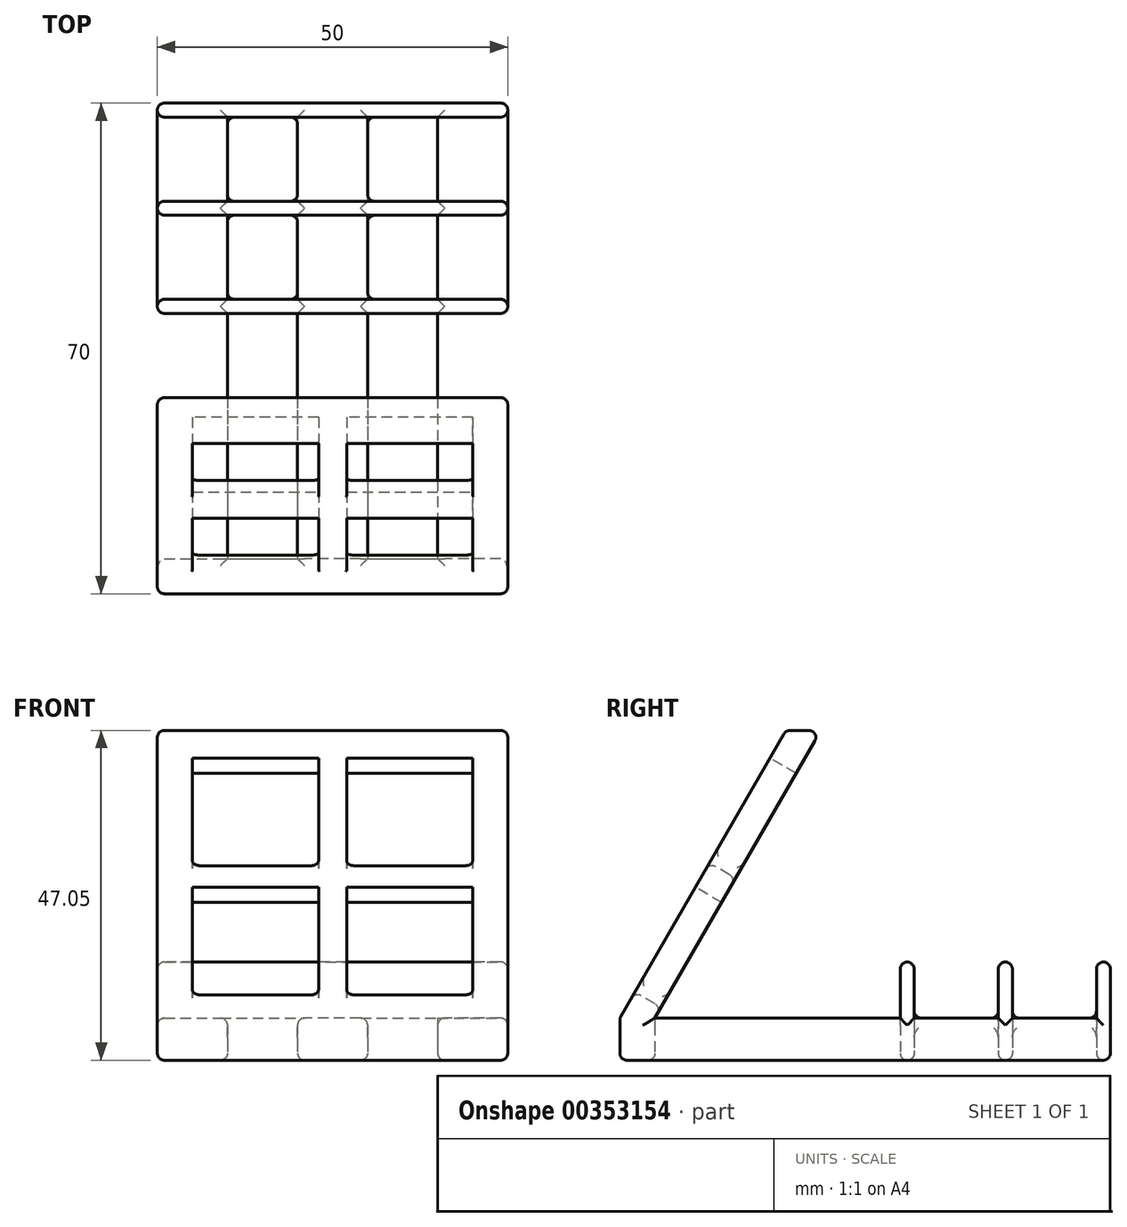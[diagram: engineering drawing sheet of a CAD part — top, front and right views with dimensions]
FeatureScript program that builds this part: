
annotation { "Feature Type Name" : "Feature", "Feature Type Description" : "" }
export const myFeature = defineFeature(function(context is Context, id is Id, definition is map)
    precondition{}
    {
        {
            var Q0;
            Q0=qCreatedBy(makeId("Top.planeOp"),FACE);
            var sketch = newSketch(context, id + "F0", { "sketchPlane" : qUnion([Q0])});
            skLineSegment(sketch, "E0.bottom", {"start": v(-23.48, 33.9) * mm, "end": v(26.52, 33.9) * mm});
            skLineSegment(sketch, "E0.top", {"start": v(-23.48, -36.1) * mm, "end": v(26.52, -36.1) * mm});
            skLineSegment(sketch, "E0.left", {"start": v(-23.48, 33.9) * mm, "end": v(-23.48, -36.1) * mm});
            skLineSegment(sketch, "E0.right", {"start": v(26.52, 33.9) * mm, "end": v(26.52, -36.1) * mm});
            skLineSegment(sketch, "E1", {"start": v(-23.48, 31.9) * mm, "end": v(26.52, 31.9) * mm});
            skLineSegment(sketch, "E2", {"start": v(-23.48, 19.9) * mm, "end": v(26.52, 19.9) * mm});
            skLineSegment(sketch, "E3", {"start": v(-23.48, 17.9) * mm, "end": v(26.52, 17.9) * mm});
            skLineSegment(sketch, "E4", {"start": v(-23.48, 5.9) * mm, "end": v(26.52, 5.9) * mm});
            skLineSegment(sketch, "E5", {"start": v(-23.48, -31.1) * mm, "end": v(26.52, -31.1) * mm});
            skLineSegment(sketch, "E6", {"start": v(-23.48, 3.9) * mm, "end": v(26.52, 3.9) * mm});
            skLineSegment(sketch, "E7", {"start": v(16.52, 33.9) * mm, "end": v(16.52, -36.1) * mm});
            skLineSegment(sketch, "E8", {"start": v(-13.48, 33.9) * mm, "end": v(-13.48, -36.1) * mm});
            skLineSegment(sketch, "E9.0", {"start": v(-3.48, 33.9) * mm, "end": v(-3.48, -36.1) * mm});
            skLineSegment(sketch, "E10.0", {"start": v(6.52, 33.9) * mm, "end": v(6.52, -36.1) * mm});
            skSolve(sketch);
        }
        {
            var Q0;
            {var subQ0=sQuery(id+"F0.wireOp",EDGE,"E9.0");var subQ1=sQuery(id+"F0.wireOp",EDGE,"E0.bottom");var subQ2=makeQuery(id+"F0.imprint","INTERSECT",VERTEX,{"derivedFrom":[subQ1,subQ0]});Q0=makeQuery(id+"F0.imprint","IMPRINT",FACE,{"disambiguationData":[TD([[makeQuery(id+"F0.imprint","IMPRINT",EDGE,{"disambiguationData":[TD([[subQ2,-1.0]])],"derivedFrom":subQ1}),-1.0]])]});}
            var Q1;
            {var subQ0=sQuery(id+"F0.wireOp",EDGE,"E9.0");var subQ1=sQuery(id+"F0.wireOp",EDGE,"E3");var subQ2=makeQuery(id+"F0.imprint","INTERSECT",VERTEX,{"derivedFrom":[subQ1,subQ0]});Q1=makeQuery(id+"F0.imprint","IMPRINT",FACE,{"disambiguationData":[TD([[makeQuery(id+"F0.imprint","IMPRINT",EDGE,{"disambiguationData":[TD([[subQ2,-1.0]])],"derivedFrom":subQ1}),-1.0]])]});}
            var Q2;
            {var subQ0=sQuery(id+"F0.wireOp",EDGE,"E10.0");var subQ1=sQuery(id+"F0.wireOp",EDGE,"E2");var subQ2=makeQuery(id+"F0.imprint","INTERSECT",VERTEX,{"derivedFrom":[subQ1,subQ0]});Q2=makeQuery(id+"F0.imprint","IMPRINT",FACE,{"disambiguationData":[TD([[makeQuery(id+"F0.imprint","IMPRINT",EDGE,{"disambiguationData":[TD([[subQ2,-1.0]])],"derivedFrom":subQ1}),-1.0]])]});}
            var Q3;
            {var subQ0=sQuery(id+"F0.wireOp",EDGE,"E5");var subQ1=sQuery(id+"F0.wireOp",EDGE,"E0.left");var subQ2=makeQuery(id+"F0.imprint","INTERSECT",VERTEX,{"derivedFrom":[subQ1,subQ0]});Q3=makeQuery(id+"F0.imprint","IMPRINT",FACE,{"disambiguationData":[TD([[makeQuery(id+"F0.imprint","IMPRINT",EDGE,{"disambiguationData":[TD([[subQ2,1.0]])],"derivedFrom":subQ1}),1.0]])]});}
            var Q4;
            {var subQ0=sQuery(id+"F0.wireOp",EDGE,"E0.left");var subQ1=sQuery(id+"F0.wireOp",EDGE,"E0.top");var subQ2=makeQuery(id+"F0.imprint","INTERSECT",VERTEX,{"derivedFrom":[subQ1,subQ0]});Q4=makeQuery(id+"F0.imprint","IMPRINT",FACE,{"disambiguationData":[TD([[makeQuery(id+"F0.imprint","IMPRINT",EDGE,{"disambiguationData":[TD([[subQ2,-1.0]])],"derivedFrom":subQ1}),1.0]])]});}
            var Q5;
            {var subQ0=sQuery(id+"F0.wireOp",EDGE,"E3");var subQ1=sQuery(id+"F0.wireOp",EDGE,"E0.left");var subQ2=makeQuery(id+"F0.imprint","INTERSECT",VERTEX,{"derivedFrom":[subQ1,subQ0]});Q5=makeQuery(id+"F0.imprint","IMPRINT",FACE,{"disambiguationData":[TD([[makeQuery(id+"F0.imprint","IMPRINT",EDGE,{"disambiguationData":[TD([[subQ2,-1.0]])],"derivedFrom":subQ1}),1.0]])]});}
            var Q6;
            {var subQ0=sQuery(id+"F0.wireOp",EDGE,"E8");var subQ1=sQuery(id+"F0.wireOp",EDGE,"E0.bottom");var subQ2=makeQuery(id+"F0.imprint","INTERSECT",VERTEX,{"derivedFrom":[subQ1,subQ0]});Q6=makeQuery(id+"F0.imprint","IMPRINT",FACE,{"disambiguationData":[TD([[makeQuery(id+"F0.imprint","IMPRINT",EDGE,{"disambiguationData":[TD([[subQ2,-1.0]])],"derivedFrom":subQ1}),-1.0]])]});}
            var Q7;
            {var subQ0=sQuery(id+"F0.wireOp",EDGE,"E2");var subQ1=sQuery(id+"F0.wireOp",EDGE,"E0.right");var subQ2=makeQuery(id+"F0.imprint","INTERSECT",VERTEX,{"derivedFrom":[subQ1,subQ0]});Q7=makeQuery(id+"F0.imprint","IMPRINT",FACE,{"disambiguationData":[TD([[makeQuery(id+"F0.imprint","IMPRINT",EDGE,{"disambiguationData":[TD([[subQ2,-1.0]])],"derivedFrom":subQ1}),-1.0]])]});}
            var Q8;
            {var subQ0=sQuery(id+"F0.wireOp",EDGE,"E4");var subQ1=sQuery(id+"F0.wireOp",EDGE,"E0.right");var subQ2=makeQuery(id+"F0.imprint","INTERSECT",VERTEX,{"derivedFrom":[subQ1,subQ0]});Q8=makeQuery(id+"F0.imprint","IMPRINT",FACE,{"disambiguationData":[TD([[makeQuery(id+"F0.imprint","IMPRINT",EDGE,{"disambiguationData":[TD([[subQ2,-1.0]])],"derivedFrom":subQ1}),-1.0]])]});}
            var Q9;
            {var subQ0=sQuery(id+"F0.wireOp",EDGE,"E3");var subQ1=sQuery(id+"F0.wireOp",EDGE,"E0.right");var subQ2=makeQuery(id+"F0.imprint","INTERSECT",VERTEX,{"derivedFrom":[subQ1,subQ0]});Q9=makeQuery(id+"F0.imprint","IMPRINT",FACE,{"disambiguationData":[TD([[makeQuery(id+"F0.imprint","IMPRINT",EDGE,{"disambiguationData":[TD([[subQ2,-1.0]])],"derivedFrom":subQ1}),-1.0]])]});}
            var Q10;
            {var subQ0=sQuery(id+"F0.wireOp",EDGE,"E2");var subQ1=sQuery(id+"F0.wireOp",EDGE,"E0.left");var subQ2=makeQuery(id+"F0.imprint","INTERSECT",VERTEX,{"derivedFrom":[subQ1,subQ0]});Q10=makeQuery(id+"F0.imprint","IMPRINT",FACE,{"disambiguationData":[TD([[makeQuery(id+"F0.imprint","IMPRINT",EDGE,{"disambiguationData":[TD([[subQ2,-1.0]])],"derivedFrom":subQ1}),1.0]])]});}
            var Q11;
            {var subQ0=sQuery(id+"F0.wireOp",EDGE,"E7");var subQ1=sQuery(id+"F0.wireOp",EDGE,"E0.top");var subQ2=makeQuery(id+"F0.imprint","INTERSECT",VERTEX,{"derivedFrom":[subQ1,subQ0]});Q11=makeQuery(id+"F0.imprint","IMPRINT",FACE,{"disambiguationData":[TD([[makeQuery(id+"F0.imprint","IMPRINT",EDGE,{"disambiguationData":[TD([[subQ2,1.0]])],"derivedFrom":subQ1}),1.0]])]});}
            var Q12;
            {var subQ0=sQuery(id+"F0.wireOp",EDGE,"E9.0");var subQ1=sQuery(id+"F0.wireOp",EDGE,"E0.top");var subQ2=makeQuery(id+"F0.imprint","INTERSECT",VERTEX,{"derivedFrom":[subQ1,subQ0]});Q12=makeQuery(id+"F0.imprint","IMPRINT",FACE,{"disambiguationData":[TD([[makeQuery(id+"F0.imprint","IMPRINT",EDGE,{"disambiguationData":[TD([[subQ2,-1.0]])],"derivedFrom":subQ1}),1.0]])]});}
            var Q13;
            {var subQ0=sQuery(id+"F0.wireOp",EDGE,"E10.0");var subQ1=sQuery(id+"F0.wireOp",EDGE,"E4");var subQ2=makeQuery(id+"F0.imprint","INTERSECT",VERTEX,{"derivedFrom":[subQ1,subQ0]});Q13=makeQuery(id+"F0.imprint","IMPRINT",FACE,{"disambiguationData":[TD([[makeQuery(id+"F0.imprint","IMPRINT",EDGE,{"disambiguationData":[TD([[subQ2,-1.0]])],"derivedFrom":subQ1}),-1.0]])]});}
            var Q14;
            {var subQ0=sQuery(id+"F0.wireOp",EDGE,"E0.right");var subQ1=sQuery(id+"F0.wireOp",EDGE,"E0.top");var subQ2=makeQuery(id+"F0.imprint","INTERSECT",VERTEX,{"derivedFrom":[subQ1,subQ0]});Q14=makeQuery(id+"F0.imprint","IMPRINT",FACE,{"disambiguationData":[TD([[makeQuery(id+"F0.imprint","IMPRINT",EDGE,{"disambiguationData":[TD([[subQ2,1.0]])],"derivedFrom":subQ1}),1.0]])]});}
            var Q15;
            {var subQ0=sQuery(id+"F0.wireOp",EDGE,"E1");var subQ1=sQuery(id+"F0.wireOp",EDGE,"E0.left");var subQ2=makeQuery(id+"F0.imprint","INTERSECT",VERTEX,{"derivedFrom":[subQ1,subQ0]});Q15=makeQuery(id+"F0.imprint","IMPRINT",FACE,{"disambiguationData":[TD([[makeQuery(id+"F0.imprint","IMPRINT",EDGE,{"disambiguationData":[TD([[subQ2,-1.0]])],"derivedFrom":subQ1}),1.0]])]});}
            var Q16;
            {var subQ0=sQuery(id+"F0.wireOp",EDGE,"E9.0");var subQ1=sQuery(id+"F0.wireOp",EDGE,"E5");var subQ2=makeQuery(id+"F0.imprint","INTERSECT",VERTEX,{"derivedFrom":[subQ1,subQ0]});Q16=makeQuery(id+"F0.imprint","IMPRINT",FACE,{"disambiguationData":[TD([[makeQuery(id+"F0.imprint","IMPRINT",EDGE,{"disambiguationData":[TD([[subQ2,-1.0]])],"derivedFrom":subQ1}),1.0]])]});}
            var Q17;
            {var subQ0=sQuery(id+"F0.wireOp",EDGE,"E8");var subQ1=sQuery(id+"F0.wireOp",EDGE,"E2");var subQ2=makeQuery(id+"F0.imprint","INTERSECT",VERTEX,{"derivedFrom":[subQ1,subQ0]});Q17=makeQuery(id+"F0.imprint","IMPRINT",FACE,{"disambiguationData":[TD([[makeQuery(id+"F0.imprint","IMPRINT",EDGE,{"disambiguationData":[TD([[subQ2,-1.0]])],"derivedFrom":subQ1}),-1.0]])]});}
            var Q18;
            {var subQ0=sQuery(id+"F0.wireOp",EDGE,"E8");var subQ1=sQuery(id+"F0.wireOp",EDGE,"E0.top");var subQ2=makeQuery(id+"F0.imprint","INTERSECT",VERTEX,{"derivedFrom":[subQ1,subQ0]});Q18=makeQuery(id+"F0.imprint","IMPRINT",FACE,{"disambiguationData":[TD([[makeQuery(id+"F0.imprint","IMPRINT",EDGE,{"disambiguationData":[TD([[subQ2,-1.0]])],"derivedFrom":subQ1}),1.0]])]});}
            var Q19;
            {var subQ0=sQuery(id+"F0.wireOp",EDGE,"E9.0");var subQ1=sQuery(id+"F0.wireOp",EDGE,"E4");var subQ2=makeQuery(id+"F0.imprint","INTERSECT",VERTEX,{"derivedFrom":[subQ1,subQ0]});Q19=makeQuery(id+"F0.imprint","IMPRINT",FACE,{"disambiguationData":[TD([[makeQuery(id+"F0.imprint","IMPRINT",EDGE,{"disambiguationData":[TD([[subQ2,-1.0]])],"derivedFrom":subQ1}),-1.0]])]});}
            var Q20;
            {var subQ0=sQuery(id+"F0.wireOp",EDGE,"E9.0");var subQ1=sQuery(id+"F0.wireOp",EDGE,"E1");var subQ2=makeQuery(id+"F0.imprint","INTERSECT",VERTEX,{"derivedFrom":[subQ1,subQ0]});Q20=makeQuery(id+"F0.imprint","IMPRINT",FACE,{"disambiguationData":[TD([[makeQuery(id+"F0.imprint","IMPRINT",EDGE,{"disambiguationData":[TD([[subQ2,-1.0]])],"derivedFrom":subQ1}),-1.0]])]});}
            var Q21;
            {var subQ0=sQuery(id+"F0.wireOp",EDGE,"E5");var subQ1=sQuery(id+"F0.wireOp",EDGE,"E0.right");var subQ2=makeQuery(id+"F0.imprint","INTERSECT",VERTEX,{"derivedFrom":[subQ1,subQ0]});Q21=makeQuery(id+"F0.imprint","IMPRINT",FACE,{"disambiguationData":[TD([[makeQuery(id+"F0.imprint","IMPRINT",EDGE,{"disambiguationData":[TD([[subQ2,1.0]])],"derivedFrom":subQ1}),-1.0]])]});}
            var Q22;
            {var subQ0=sQuery(id+"F0.wireOp",EDGE,"E4");var subQ1=sQuery(id+"F0.wireOp",EDGE,"E0.left");var subQ2=makeQuery(id+"F0.imprint","INTERSECT",VERTEX,{"derivedFrom":[subQ1,subQ0]});Q22=makeQuery(id+"F0.imprint","IMPRINT",FACE,{"disambiguationData":[TD([[makeQuery(id+"F0.imprint","IMPRINT",EDGE,{"disambiguationData":[TD([[subQ2,-1.0]])],"derivedFrom":subQ1}),1.0]])]});}
            var Q23;
            {var subQ0=sQuery(id+"F0.wireOp",EDGE,"E8");var subQ1=sQuery(id+"F0.wireOp",EDGE,"E4");var subQ2=makeQuery(id+"F0.imprint","INTERSECT",VERTEX,{"derivedFrom":[subQ1,subQ0]});Q23=makeQuery(id+"F0.imprint","IMPRINT",FACE,{"disambiguationData":[TD([[makeQuery(id+"F0.imprint","IMPRINT",EDGE,{"disambiguationData":[TD([[subQ2,-1.0]])],"derivedFrom":subQ1}),-1.0]])]});}
            var Q24;
            {var subQ0=sQuery(id+"F0.wireOp",EDGE,"E9.0");var subQ1=sQuery(id+"F0.wireOp",EDGE,"E2");var subQ2=makeQuery(id+"F0.imprint","INTERSECT",VERTEX,{"derivedFrom":[subQ1,subQ0]});Q24=makeQuery(id+"F0.imprint","IMPRINT",FACE,{"disambiguationData":[TD([[makeQuery(id+"F0.imprint","IMPRINT",EDGE,{"disambiguationData":[TD([[subQ2,-1.0]])],"derivedFrom":subQ1}),-1.0]])]});}
            var Q25;
            {var subQ0=sQuery(id+"F0.wireOp",EDGE,"E1");var subQ1=sQuery(id+"F0.wireOp",EDGE,"E0.right");var subQ2=makeQuery(id+"F0.imprint","INTERSECT",VERTEX,{"derivedFrom":[subQ1,subQ0]});Q25=makeQuery(id+"F0.imprint","IMPRINT",FACE,{"disambiguationData":[TD([[makeQuery(id+"F0.imprint","IMPRINT",EDGE,{"disambiguationData":[TD([[subQ2,-1.0]])],"derivedFrom":subQ1}),-1.0]])]});}
            var Q26;
            {var subQ0=sQuery(id+"F0.wireOp",EDGE,"E0.left");var subQ1=sQuery(id+"F0.wireOp",EDGE,"E0.bottom");var subQ2=makeQuery(id+"F0.imprint","INTERSECT",VERTEX,{"derivedFrom":[subQ1,subQ0]});Q26=makeQuery(id+"F0.imprint","IMPRINT",FACE,{"disambiguationData":[TD([[makeQuery(id+"F0.imprint","IMPRINT",EDGE,{"disambiguationData":[TD([[subQ2,-1.0]])],"derivedFrom":subQ1}),-1.0]])]});}
            var Q27;
            {var subQ0=sQuery(id+"F0.wireOp",EDGE,"E0.right");var subQ1=sQuery(id+"F0.wireOp",EDGE,"E0.bottom");var subQ2=makeQuery(id+"F0.imprint","INTERSECT",VERTEX,{"derivedFrom":[subQ1,subQ0]});Q27=makeQuery(id+"F0.imprint","IMPRINT",FACE,{"disambiguationData":[TD([[makeQuery(id+"F0.imprint","IMPRINT",EDGE,{"disambiguationData":[TD([[subQ2,1.0]])],"derivedFrom":subQ1}),-1.0]])]});}
            var Q28;
            {var subQ0=sQuery(id+"F0.wireOp",EDGE,"E7");var subQ1=sQuery(id+"F0.wireOp",EDGE,"E0.bottom");var subQ2=makeQuery(id+"F0.imprint","INTERSECT",VERTEX,{"derivedFrom":[subQ1,subQ0]});Q28=makeQuery(id+"F0.imprint","IMPRINT",FACE,{"disambiguationData":[TD([[makeQuery(id+"F0.imprint","IMPRINT",EDGE,{"disambiguationData":[TD([[subQ2,1.0]])],"derivedFrom":subQ1}),-1.0]])]});}
            extrude(context, id + "F1", {"entities" : qUnion([Q0, Q1, Q2, Q3, Q4, Q5, Q6, Q7, Q8, Q9, Q10, Q11, Q12, Q13, Q14, Q15, Q16, Q17, Q18, Q19, Q20, Q21, Q22, Q23, Q24, Q25, Q26, Q27, Q28]), "depth" : 6 * mm});
        }
        {
            var Q0;
            {var subQ0=sQuery(id+"F0.wireOp",EDGE,"E8");var subQ1=sQuery(id+"F0.wireOp",EDGE,"E0.bottom");var subQ2=makeQuery(id+"F0.imprint","INTERSECT",VERTEX,{"derivedFrom":[subQ1,subQ0]});Q0=makeQuery(id+"F0.imprint","IMPRINT",FACE,{"disambiguationData":[TD([[makeQuery(id+"F0.imprint","IMPRINT",EDGE,{"disambiguationData":[TD([[subQ2,-1.0]])],"derivedFrom":subQ1}),-1.0]])]});}
            var Q1;
            {var subQ0=sQuery(id+"F0.wireOp",EDGE,"E0.left");var subQ1=sQuery(id+"F0.wireOp",EDGE,"E0.bottom");var subQ2=makeQuery(id+"F0.imprint","INTERSECT",VERTEX,{"derivedFrom":[subQ1,subQ0]});Q1=makeQuery(id+"F0.imprint","IMPRINT",FACE,{"disambiguationData":[TD([[makeQuery(id+"F0.imprint","IMPRINT",EDGE,{"disambiguationData":[TD([[subQ2,-1.0]])],"derivedFrom":subQ1}),-1.0]])]});}
            var Q2;
            {var subQ0=sQuery(id+"F0.wireOp",EDGE,"E7");var subQ1=sQuery(id+"F0.wireOp",EDGE,"E0.bottom");var subQ2=makeQuery(id+"F0.imprint","INTERSECT",VERTEX,{"derivedFrom":[subQ1,subQ0]});Q2=makeQuery(id+"F0.imprint","IMPRINT",FACE,{"disambiguationData":[TD([[makeQuery(id+"F0.imprint","IMPRINT",EDGE,{"disambiguationData":[TD([[subQ2,1.0]])],"derivedFrom":subQ1}),-1.0]])]});}
            var Q3;
            {var subQ0=sQuery(id+"F0.wireOp",EDGE,"E9.0");var subQ1=sQuery(id+"F0.wireOp",EDGE,"E0.bottom");var subQ2=makeQuery(id+"F0.imprint","INTERSECT",VERTEX,{"derivedFrom":[subQ1,subQ0]});Q3=makeQuery(id+"F0.imprint","IMPRINT",FACE,{"disambiguationData":[TD([[makeQuery(id+"F0.imprint","IMPRINT",EDGE,{"disambiguationData":[TD([[subQ2,-1.0]])],"derivedFrom":subQ1}),-1.0]])]});}
            var Q4;
            {var subQ0=sQuery(id+"F0.wireOp",EDGE,"E0.right");var subQ1=sQuery(id+"F0.wireOp",EDGE,"E0.bottom");var subQ2=makeQuery(id+"F0.imprint","INTERSECT",VERTEX,{"derivedFrom":[subQ1,subQ0]});Q4=makeQuery(id+"F0.imprint","IMPRINT",FACE,{"disambiguationData":[TD([[makeQuery(id+"F0.imprint","IMPRINT",EDGE,{"disambiguationData":[TD([[subQ2,1.0]])],"derivedFrom":subQ1}),-1.0]])]});}
            var Q5;
            {var subQ0=sQuery(id+"F0.wireOp",EDGE,"E9.0");var subQ1=sQuery(id+"F0.wireOp",EDGE,"E2");var subQ2=makeQuery(id+"F0.imprint","INTERSECT",VERTEX,{"derivedFrom":[subQ1,subQ0]});Q5=makeQuery(id+"F0.imprint","IMPRINT",FACE,{"disambiguationData":[TD([[makeQuery(id+"F0.imprint","IMPRINT",EDGE,{"disambiguationData":[TD([[subQ2,-1.0]])],"derivedFrom":subQ1}),-1.0]])]});}
            var Q6;
            {var subQ0=sQuery(id+"F0.wireOp",EDGE,"E10.0");var subQ1=sQuery(id+"F0.wireOp",EDGE,"E2");var subQ2=makeQuery(id+"F0.imprint","INTERSECT",VERTEX,{"derivedFrom":[subQ1,subQ0]});Q6=makeQuery(id+"F0.imprint","IMPRINT",FACE,{"disambiguationData":[TD([[makeQuery(id+"F0.imprint","IMPRINT",EDGE,{"disambiguationData":[TD([[subQ2,-1.0]])],"derivedFrom":subQ1}),-1.0]])]});}
            var Q7;
            {var subQ0=sQuery(id+"F0.wireOp",EDGE,"E2");var subQ1=sQuery(id+"F0.wireOp",EDGE,"E0.right");var subQ2=makeQuery(id+"F0.imprint","INTERSECT",VERTEX,{"derivedFrom":[subQ1,subQ0]});Q7=makeQuery(id+"F0.imprint","IMPRINT",FACE,{"disambiguationData":[TD([[makeQuery(id+"F0.imprint","IMPRINT",EDGE,{"disambiguationData":[TD([[subQ2,-1.0]])],"derivedFrom":subQ1}),-1.0]])]});}
            var Q8;
            {var subQ0=sQuery(id+"F0.wireOp",EDGE,"E8");var subQ1=sQuery(id+"F0.wireOp",EDGE,"E2");var subQ2=makeQuery(id+"F0.imprint","INTERSECT",VERTEX,{"derivedFrom":[subQ1,subQ0]});Q8=makeQuery(id+"F0.imprint","IMPRINT",FACE,{"disambiguationData":[TD([[makeQuery(id+"F0.imprint","IMPRINT",EDGE,{"disambiguationData":[TD([[subQ2,-1.0]])],"derivedFrom":subQ1}),-1.0]])]});}
            var Q9;
            {var subQ0=sQuery(id+"F0.wireOp",EDGE,"E2");var subQ1=sQuery(id+"F0.wireOp",EDGE,"E0.left");var subQ2=makeQuery(id+"F0.imprint","INTERSECT",VERTEX,{"derivedFrom":[subQ1,subQ0]});Q9=makeQuery(id+"F0.imprint","IMPRINT",FACE,{"disambiguationData":[TD([[makeQuery(id+"F0.imprint","IMPRINT",EDGE,{"disambiguationData":[TD([[subQ2,-1.0]])],"derivedFrom":subQ1}),1.0]])]});}
            var Q10;
            {var subQ0=sQuery(id+"F0.wireOp",EDGE,"E4");var subQ1=sQuery(id+"F0.wireOp",EDGE,"E0.left");var subQ2=makeQuery(id+"F0.imprint","INTERSECT",VERTEX,{"derivedFrom":[subQ1,subQ0]});Q10=makeQuery(id+"F0.imprint","IMPRINT",FACE,{"disambiguationData":[TD([[makeQuery(id+"F0.imprint","IMPRINT",EDGE,{"disambiguationData":[TD([[subQ2,-1.0]])],"derivedFrom":subQ1}),1.0]])]});}
            var Q11;
            {var subQ0=sQuery(id+"F0.wireOp",EDGE,"E8");var subQ1=sQuery(id+"F0.wireOp",EDGE,"E4");var subQ2=makeQuery(id+"F0.imprint","INTERSECT",VERTEX,{"derivedFrom":[subQ1,subQ0]});Q11=makeQuery(id+"F0.imprint","IMPRINT",FACE,{"disambiguationData":[TD([[makeQuery(id+"F0.imprint","IMPRINT",EDGE,{"disambiguationData":[TD([[subQ2,-1.0]])],"derivedFrom":subQ1}),-1.0]])]});}
            var Q12;
            {var subQ0=sQuery(id+"F0.wireOp",EDGE,"E9.0");var subQ1=sQuery(id+"F0.wireOp",EDGE,"E4");var subQ2=makeQuery(id+"F0.imprint","INTERSECT",VERTEX,{"derivedFrom":[subQ1,subQ0]});Q12=makeQuery(id+"F0.imprint","IMPRINT",FACE,{"disambiguationData":[TD([[makeQuery(id+"F0.imprint","IMPRINT",EDGE,{"disambiguationData":[TD([[subQ2,-1.0]])],"derivedFrom":subQ1}),-1.0]])]});}
            var Q13;
            {var subQ0=sQuery(id+"F0.wireOp",EDGE,"E10.0");var subQ1=sQuery(id+"F0.wireOp",EDGE,"E4");var subQ2=makeQuery(id+"F0.imprint","INTERSECT",VERTEX,{"derivedFrom":[subQ1,subQ0]});Q13=makeQuery(id+"F0.imprint","IMPRINT",FACE,{"disambiguationData":[TD([[makeQuery(id+"F0.imprint","IMPRINT",EDGE,{"disambiguationData":[TD([[subQ2,-1.0]])],"derivedFrom":subQ1}),-1.0]])]});}
            var Q14;
            {var subQ0=sQuery(id+"F0.wireOp",EDGE,"E4");var subQ1=sQuery(id+"F0.wireOp",EDGE,"E0.right");var subQ2=makeQuery(id+"F0.imprint","INTERSECT",VERTEX,{"derivedFrom":[subQ1,subQ0]});Q14=makeQuery(id+"F0.imprint","IMPRINT",FACE,{"disambiguationData":[TD([[makeQuery(id+"F0.imprint","IMPRINT",EDGE,{"disambiguationData":[TD([[subQ2,-1.0]])],"derivedFrom":subQ1}),-1.0]])]});}
            extrude(context, id + "F2", {"entities" : qUnion([Q0, Q1, Q2, Q3, Q4, Q5, Q6, Q7, Q8, Q9, Q10, Q11, Q12, Q13, Q14]), "depth" : 14 * mm});
        }
        {
            var Q0;
            Q0=makeQuery(id+"F1.opExtrude","SWEPT_FACE",FACE,{"disambiguationData":[OSD([sQuery(id+"F0.wireOp",EDGE,"E0.left")])]});
            var sketch = newSketch(context, id + "F3", { "sketchPlane" : qUnion([Q0])});
            skLineSegment(sketch, "E11", {"start": v(36.1, 6) * mm, "end": v(12.4, 47.05) * mm});
            skSolve(sketch);
        }
        {
            var Q0;
            Q0=qCreatedBy(makeId("Top.planeOp"),FACE);
            var Q1;
            Q1=sQuery(id+"F3.wireOp",VERTEX,"E11.end");
            cPlane(context, id + "F4", {"entities" : qUnion([Q0, Q1]), "cplaneType" : CPlaneType.PLANE_POINT, "offset" : 25 * mm, "width" : 150 * mm, "height" : 150 * mm});
        }
        {
            var Q0;
            Q0=qCreatedBy(id+"F4.planeOp",FACE);
            var sketch = newSketch(context, id + "F5", { "sketchPlane" : qUnion([Q0])});
            skLineSegment(sketch, "E12.0", {"start": v(-23.48, -7.4) * mm, "end": v(-23.48, -12.4) * mm});
            skLineSegment(sketch, "E12.1", {"start": v(26.52, -7.4) * mm, "end": v(26.52, -12.4) * mm});
            skLineSegment(sketch, "E13", {"start": v(-23.48, -12.4) * mm, "end": v(26.52, -12.4) * mm});
            skLineSegment(sketch, "E14", {"start": v(26.52, -7.4) * mm, "end": v(-23.48, -7.4) * mm});
            skPoint(sketch, "E15.orphan", {"position": v(-23.48, 33.9) * mm});
            skPoint(sketch, "E16.orphan", {"position": v(-23.48, -36.1) * mm});
            skPoint(sketch, "E17.orphan", {"position": v(26.52, -36.1) * mm});
            skPoint(sketch, "E18.orphan", {"position": v(26.52, 33.9) * mm});
            skSolve(sketch);
        }
        {
            var Q0;
            Q0=makeQuery(id+"F1.opExtrude","CAP_FACE",FACE,{"disambiguationData":[OSD([sQuery(id+"F0.wireOp",EDGE,"E0.bottom"),sQuery(id+"F0.wireOp",EDGE,"E0.top"),sQuery(id+"F0.wireOp",EDGE,"E0.left"),sQuery(id+"F0.wireOp",EDGE,"E0.right"),sQuery(id+"F0.wireOp",EDGE,"E1"),sQuery(id+"F0.wireOp",EDGE,"E2"),sQuery(id+"F0.wireOp",EDGE,"E3"),sQuery(id+"F0.wireOp",EDGE,"E4"),sQuery(id+"F0.wireOp",EDGE,"E5"),sQuery(id+"F0.wireOp",EDGE,"E6"),sQuery(id+"F0.wireOp",EDGE,"E7"),sQuery(id+"F0.wireOp",EDGE,"E8"),sQuery(id+"F0.wireOp",EDGE,"E9.0"),sQuery(id+"F0.wireOp",EDGE,"E10.0")])],"isStart":false});
            var sketch = newSketch(context, id + "F6", { "sketchPlane" : qUnion([Q0])});
            skLineSegment(sketch, "E19.0", {"start": v(-23.48, -31.1) * mm, "end": v(26.52, -31.1) * mm});
            skLineSegment(sketch, "E19.1", {"start": v(-23.48, -36.1) * mm, "end": v(26.52, -36.1) * mm});
            skLineSegment(sketch, "E19.2", {"start": v(-23.48, -31.1) * mm, "end": v(-23.48, -36.1) * mm});
            skLineSegment(sketch, "E19.3", {"start": v(26.52, -31.1) * mm, "end": v(26.52, -36.1) * mm});
            skPoint(sketch, "E20.orphan", {"position": v(-23.48, 33.9) * mm});
            skPoint(sketch, "E21.orphan", {"position": v(26.52, 33.9) * mm});
            skSolve(sketch);
        }
        {
            var Q0;
            Q0=makeQuery(id+"F5.imprint","IMPRINT",FACE,{"disambiguationData":[TD([[makeQuery(id+"F5.imprint","IMPRINT",EDGE,{"derivedFrom":sQuery(id+"F5.wireOp",EDGE,"E12.0")}),1.0]])]});
            var Q1;
            Q1=makeQuery(id+"F6.imprint","IMPRINT",FACE,{"disambiguationData":[TD([[makeQuery(id+"F6.imprint","IMPRINT",EDGE,{"derivedFrom":sQuery(id+"F6.wireOp",EDGE,"E19.1")}),1.0]])]});
            var Q2;
            Q2=sQuery(id+"F3.wireOp",EDGE,"E11");
            loft(context, id + "F7", {"sheetProfilesArray" : [{ "sheetProfileEntities" : qUnion([Q0]) }, { "sheetProfileEntities" : qUnion([Q1]) }], "guidesArray" : [{ "guideEntities" : qUnion([Q2]), "guideDerivativeType" : LoftGuideDerivativeType.DEFAULT, "guideDerivativeMagnitude" : 1 }]});
        }
        {
            var Q0;
            Q0=makeQuery(id+"F2.opExtrude","SWEPT_BODY",BODY,{"disambiguationData":[OSD([sQuery(id+"F0.wireOp",EDGE,"E0.left"),sQuery(id+"F0.wireOp",EDGE,"E0.right"),sQuery(id+"F0.wireOp",EDGE,"E4"),sQuery(id+"F0.wireOp",EDGE,"E6")])]});
            var Q1;
            Q1=makeQuery(id+"F2.opExtrude","SWEPT_BODY",BODY,{"disambiguationData":[OSD([sQuery(id+"F0.wireOp",EDGE,"E0.left"),sQuery(id+"F0.wireOp",EDGE,"E0.right"),sQuery(id+"F0.wireOp",EDGE,"E2"),sQuery(id+"F0.wireOp",EDGE,"E3")])]});
            var Q2;
            Q2=makeQuery(id+"F7.opLoft","SWEPT_BODY",BODY,{"disambiguationData":[OSD([makeQuery(id+"F5.imprint","IMPRINT",FACE,{"disambiguationData":[TD([[makeQuery(id+"F5.imprint","IMPRINT",EDGE,{"derivedFrom":sQuery(id+"F5.wireOp",EDGE,"E12.0")}),1.0]])]}),makeQuery(id+"F6.imprint","IMPRINT",FACE,{"disambiguationData":[TD([[makeQuery(id+"F6.imprint","IMPRINT",EDGE,{"derivedFrom":sQuery(id+"F6.wireOp",EDGE,"E19.1")}),1.0]])]})])]});
            var Q3;
            Q3=makeQuery(id+"F1.opExtrude","SWEPT_BODY",BODY,{"disambiguationData":[OSD([sQuery(id+"F0.wireOp",EDGE,"E0.bottom"),sQuery(id+"F0.wireOp",EDGE,"E0.top"),sQuery(id+"F0.wireOp",EDGE,"E0.left"),sQuery(id+"F0.wireOp",EDGE,"E0.right"),sQuery(id+"F0.wireOp",EDGE,"E1"),sQuery(id+"F0.wireOp",EDGE,"E2"),sQuery(id+"F0.wireOp",EDGE,"E3"),sQuery(id+"F0.wireOp",EDGE,"E4"),sQuery(id+"F0.wireOp",EDGE,"E5"),sQuery(id+"F0.wireOp",EDGE,"E6"),sQuery(id+"F0.wireOp",EDGE,"E7"),sQuery(id+"F0.wireOp",EDGE,"E8"),sQuery(id+"F0.wireOp",EDGE,"E9.0"),sQuery(id+"F0.wireOp",EDGE,"E10.0")])]});
            var Q4;
            Q4=makeQuery(id+"F2.opExtrude","SWEPT_BODY",BODY,{"disambiguationData":[OSD([sQuery(id+"F0.wireOp",EDGE,"E0.bottom"),sQuery(id+"F0.wireOp",EDGE,"E0.left"),sQuery(id+"F0.wireOp",EDGE,"E0.right"),sQuery(id+"F0.wireOp",EDGE,"E1")])]});
            booleanBodies(context, id + "F8", {"operationType" : BooleanOperationType.UNION, "tools" : qUnion([Q0, Q1, Q2, Q3, Q4])});
        }
        {
            var Q0;
            Q0=makeQuery(id+"F7.opLoft","CAP_FACE",FACE,{"disambiguationData":[OSD([makeQuery(id+"F5.imprint","IMPRINT",FACE,{"disambiguationData":[TD([[makeQuery(id+"F5.imprint","IMPRINT",EDGE,{"derivedFrom":sQuery(id+"F5.wireOp",EDGE,"E12.0")}),1.0]])]})])],"isStart":true});
            var Q1;
            Q1=makeQuery(id+"F2.opExtrude","CAP_FACE",FACE,{"disambiguationData":[OSD([sQuery(id+"F0.wireOp",EDGE,"E0.bottom"),sQuery(id+"F0.wireOp",EDGE,"E0.left"),sQuery(id+"F0.wireOp",EDGE,"E0.right"),sQuery(id+"F0.wireOp",EDGE,"E1")])],"isStart":false});
            var Q2;
            Q2=makeQuery(id+"F2.opExtrude","CAP_FACE",FACE,{"disambiguationData":[OSD([sQuery(id+"F0.wireOp",EDGE,"E0.left"),sQuery(id+"F0.wireOp",EDGE,"E0.right"),sQuery(id+"F0.wireOp",EDGE,"E4"),sQuery(id+"F0.wireOp",EDGE,"E6")])],"isStart":false});
            var Q3;
            Q3=makeQuery(id+"F7.opLoft","SWEPT_FACE",FACE,{"disambiguationData":[OSD([sQuery(id+"F5.wireOp",EDGE,"E12.0"),sQuery(id+"F5.wireOp",EDGE,"E12.1"),sQuery(id+"F5.wireOp",EDGE,"E13"),sQuery(id+"F6.wireOp",EDGE,"E19.1"),sQuery(id+"F6.wireOp",EDGE,"E19.2"),sQuery(id+"F6.wireOp",EDGE,"E19.3")])]});
            var Q4;
            {var subQ0=sQuery(id+"F0.wireOp",EDGE,"E0.right");Q4=makeQuery(id+"F8.opBoolean","MERGE",FACE,{"derivedFrom":[makeQuery(id+"F1.opExtrude","SWEPT_FACE",FACE,{"disambiguationData":[OSD([subQ0])]}),makeQuery(id+"F2.opExtrude","SWEPT_FACE",FACE,{"disambiguationData":[OSD([subQ0]),TDD([makeQuery(id+"F0.imprint","IMPRINT",EDGE,{"disambiguationData":[TD([[makeQuery(id+"F0.imprint","INTERSECT",VERTEX,{"derivedFrom":[sQuery(id+"F0.wireOp",EDGE,"E0.bottom"),subQ0]}),-1.0]])],"derivedFrom":subQ0})])]}),makeQuery(id+"F2.opExtrude","SWEPT_FACE",FACE,{"disambiguationData":[OSD([subQ0]),TDD([makeQuery(id+"F0.imprint","IMPRINT",EDGE,{"disambiguationData":[TD([[makeQuery(id+"F0.imprint","INTERSECT",VERTEX,{"derivedFrom":[subQ0,sQuery(id+"F0.wireOp",EDGE,"E2")]}),-1.0]])],"derivedFrom":subQ0})])]}),makeQuery(id+"F2.opExtrude","SWEPT_FACE",FACE,{"disambiguationData":[OSD([subQ0]),TDD([makeQuery(id+"F0.imprint","IMPRINT",EDGE,{"disambiguationData":[TD([[makeQuery(id+"F0.imprint","INTERSECT",VERTEX,{"derivedFrom":[subQ0,sQuery(id+"F0.wireOp",EDGE,"E4")]}),-1.0]])],"derivedFrom":subQ0})])]}),makeQuery(id+"F7.opLoft","SWEPT_FACE",FACE,{"disambiguationData":[OSD([subQ0,sQuery(id+"F5.wireOp",EDGE,"E12.1"),sQuery(id+"F5.wireOp",EDGE,"E13"),sQuery(id+"F5.wireOp",EDGE,"E14"),sQuery(id+"F6.wireOp",EDGE,"E19.0"),sQuery(id+"F6.wireOp",EDGE,"E19.1"),sQuery(id+"F6.wireOp",EDGE,"E19.3")])]})]});}
            var Q5;
            {var subQ0=sQuery(id+"F0.wireOp",EDGE,"E0.left");Q5=makeQuery(id+"F8.opBoolean","MERGE",FACE,{"derivedFrom":[makeQuery(id+"F1.opExtrude","SWEPT_FACE",FACE,{"disambiguationData":[OSD([subQ0])]}),makeQuery(id+"F2.opExtrude","SWEPT_FACE",FACE,{"disambiguationData":[OSD([subQ0]),TDD([makeQuery(id+"F0.imprint","IMPRINT",EDGE,{"disambiguationData":[TD([[makeQuery(id+"F0.imprint","INTERSECT",VERTEX,{"derivedFrom":[sQuery(id+"F0.wireOp",EDGE,"E0.bottom"),subQ0]}),-1.0]])],"derivedFrom":subQ0})])]}),makeQuery(id+"F2.opExtrude","SWEPT_FACE",FACE,{"disambiguationData":[OSD([subQ0]),TDD([makeQuery(id+"F0.imprint","IMPRINT",EDGE,{"disambiguationData":[TD([[makeQuery(id+"F0.imprint","INTERSECT",VERTEX,{"derivedFrom":[subQ0,sQuery(id+"F0.wireOp",EDGE,"E2")]}),-1.0]])],"derivedFrom":subQ0})])]}),makeQuery(id+"F2.opExtrude","SWEPT_FACE",FACE,{"disambiguationData":[OSD([subQ0]),TDD([makeQuery(id+"F0.imprint","IMPRINT",EDGE,{"disambiguationData":[TD([[makeQuery(id+"F0.imprint","INTERSECT",VERTEX,{"derivedFrom":[subQ0,sQuery(id+"F0.wireOp",EDGE,"E4")]}),-1.0]])],"derivedFrom":subQ0})])]}),makeQuery(id+"F7.opLoft","SWEPT_FACE",FACE,{"disambiguationData":[OSD([subQ0,sQuery(id+"F5.wireOp",EDGE,"E12.0"),sQuery(id+"F5.wireOp",EDGE,"E13"),sQuery(id+"F5.wireOp",EDGE,"E14"),sQuery(id+"F6.wireOp",EDGE,"E19.0"),sQuery(id+"F6.wireOp",EDGE,"E19.1"),sQuery(id+"F6.wireOp",EDGE,"E19.2")])]})]});}
            var Q6;
            Q6=makeQuery(id+"F2.opExtrude","CAP_FACE",FACE,{"disambiguationData":[OSD([sQuery(id+"F0.wireOp",EDGE,"E0.left"),sQuery(id+"F0.wireOp",EDGE,"E0.right"),sQuery(id+"F0.wireOp",EDGE,"E2"),sQuery(id+"F0.wireOp",EDGE,"E3")])],"isStart":false});
            var Q7;
            {var subQ0=sQuery(id+"F0.wireOp",EDGE,"E2");var subQ1=sQuery(id+"F0.wireOp",EDGE,"E0.left");var subQ2=sQuery(id+"F0.wireOp",EDGE,"E3");var subQ3=sQuery(id+"F0.wireOp",EDGE,"E8");var subQ4=sQuery(id+"F0.wireOp",EDGE,"E4");var subQ5=sQuery(id+"F0.wireOp",EDGE,"E6");var subQ6=sQuery(id+"F0.wireOp",EDGE,"E0.bottom");var subQ7=sQuery(id+"F0.wireOp",EDGE,"E1");Q7=makeQuery(id+"F8.opBoolean","SPLIT",FACE,{"disambiguationData":[TD([makeQuery(id+"F1.opExtrude","SWEPT_FACE",FACE,{"disambiguationData":[OSD([subQ3]),TDD([makeQuery(id+"F0.imprint","IMPRINT",EDGE,{"disambiguationData":[TD([[makeQuery(id+"F0.imprint","INTERSECT",VERTEX,{"derivedFrom":[subQ2,subQ3]}),-1.0]])],"derivedFrom":subQ3})])]})])],"derivedFrom":makeQuery(id+"F1.opExtrude","CAP_FACE",FACE,{"disambiguationData":[OSD([subQ6,sQuery(id+"F0.wireOp",EDGE,"E0.top"),subQ1,sQuery(id+"F0.wireOp",EDGE,"E0.right"),subQ7,subQ0,subQ2,subQ4,sQuery(id+"F0.wireOp",EDGE,"E5"),subQ5,sQuery(id+"F0.wireOp",EDGE,"E7"),subQ3,sQuery(id+"F0.wireOp",EDGE,"E9.0"),sQuery(id+"F0.wireOp",EDGE,"E10.0")])],"isStart":false})});}
            var Q8;
            {var subQ0=sQuery(id+"F0.wireOp",EDGE,"E10.0");var subQ1=sQuery(id+"F0.wireOp",EDGE,"E1");var subQ2=sQuery(id+"F0.wireOp",EDGE,"E7");var subQ3=sQuery(id+"F0.wireOp",EDGE,"E0.left");var subQ4=sQuery(id+"F0.wireOp",EDGE,"E0.bottom");var subQ5=sQuery(id+"F0.wireOp",EDGE,"E2");var subQ6=sQuery(id+"F0.wireOp",EDGE,"E8");var subQ7=makeQuery(id+"F0.imprint","INTERSECT",VERTEX,{"derivedFrom":[subQ1,subQ6]});var subQ8=sQuery(id+"F0.wireOp",EDGE,"E9.0");var subQ9=sQuery(id+"F0.wireOp",EDGE,"E3");var subQ10=sQuery(id+"F0.wireOp",EDGE,"E4");var subQ11=sQuery(id+"F0.wireOp",EDGE,"E6");Q8=makeQuery(id+"F8.opBoolean","SPLIT",FACE,{"disambiguationData":[TD([makeQuery(id+"F1.opExtrude","SWEPT_FACE",FACE,{"disambiguationData":[OSD([subQ6]),TDD([makeQuery(id+"F0.imprint","IMPRINT",EDGE,{"disambiguationData":[TD([[subQ7,-1.0]])],"derivedFrom":subQ6})])]})])],"derivedFrom":makeQuery(id+"F1.opExtrude","CAP_FACE",FACE,{"disambiguationData":[OSD([subQ4,sQuery(id+"F0.wireOp",EDGE,"E0.top"),subQ3,sQuery(id+"F0.wireOp",EDGE,"E0.right"),subQ1,subQ5,subQ9,subQ10,sQuery(id+"F0.wireOp",EDGE,"E5"),subQ11,subQ2,subQ6,subQ8,subQ0])],"isStart":false})});}
            var Q9;
            {var subQ0=sQuery(id+"F0.wireOp",EDGE,"E9.0");var subQ1=sQuery(id+"F0.wireOp",EDGE,"E1");var subQ2=makeQuery(id+"F0.imprint","INTERSECT",VERTEX,{"derivedFrom":[subQ1,subQ0]});var subQ3=sQuery(id+"F0.wireOp",EDGE,"E2");var subQ4=sQuery(id+"F0.wireOp",EDGE,"E10.0");var subQ6=sQuery(id+"F0.wireOp",EDGE,"E7");var subQ7=sQuery(id+"F0.wireOp",EDGE,"E8");Q9=makeQuery(id+"F8.opBoolean","SPLIT",FACE,{"disambiguationData":[TD([makeQuery(id+"F1.opExtrude","SWEPT_FACE",FACE,{"disambiguationData":[OSD([subQ0]),TDD([makeQuery(id+"F0.imprint","IMPRINT",EDGE,{"disambiguationData":[TD([[subQ2,-1.0]])],"derivedFrom":subQ0})])]})])],"derivedFrom":makeQuery(id+"F1.opExtrude","CAP_FACE",FACE,{"disambiguationData":[OSD([sQuery(id+"F0.wireOp",EDGE,"E0.bottom"),sQuery(id+"F0.wireOp",EDGE,"E0.top"),sQuery(id+"F0.wireOp",EDGE,"E0.left"),sQuery(id+"F0.wireOp",EDGE,"E0.right"),subQ1,subQ3,sQuery(id+"F0.wireOp",EDGE,"E3"),sQuery(id+"F0.wireOp",EDGE,"E4"),sQuery(id+"F0.wireOp",EDGE,"E5"),sQuery(id+"F0.wireOp",EDGE,"E6"),subQ6,subQ7,subQ0,subQ4])],"isStart":false})});}
            var Q10;
            {var subQ0=sQuery(id+"F0.wireOp",EDGE,"E9.0");var subQ1=sQuery(id+"F0.wireOp",EDGE,"E3");var subQ2=sQuery(id+"F0.wireOp",EDGE,"E4");var subQ3=sQuery(id+"F0.wireOp",EDGE,"E10.0");Q10=makeQuery(id+"F8.opBoolean","SPLIT",FACE,{"disambiguationData":[TD([makeQuery(id+"F1.opExtrude","SWEPT_FACE",FACE,{"disambiguationData":[OSD([subQ0]),TDD([makeQuery(id+"F0.imprint","IMPRINT",EDGE,{"disambiguationData":[TD([[makeQuery(id+"F0.imprint","INTERSECT",VERTEX,{"derivedFrom":[subQ1,subQ0]}),-1.0]])],"derivedFrom":subQ0})])]})])],"derivedFrom":makeQuery(id+"F1.opExtrude","CAP_FACE",FACE,{"disambiguationData":[OSD([sQuery(id+"F0.wireOp",EDGE,"E0.bottom"),sQuery(id+"F0.wireOp",EDGE,"E0.top"),sQuery(id+"F0.wireOp",EDGE,"E0.left"),sQuery(id+"F0.wireOp",EDGE,"E0.right"),sQuery(id+"F0.wireOp",EDGE,"E1"),sQuery(id+"F0.wireOp",EDGE,"E2"),subQ1,subQ2,sQuery(id+"F0.wireOp",EDGE,"E5"),sQuery(id+"F0.wireOp",EDGE,"E6"),sQuery(id+"F0.wireOp",EDGE,"E7"),sQuery(id+"F0.wireOp",EDGE,"E8"),subQ0,subQ3])],"isStart":false})});}
            fillet(context, id + "F9", {"entities" : qUnion([Q0, Q1, Q2, Q3, Q4, Q5, Q6, Q7, Q8, Q9, Q10]), "radius" : 1 * mm, "tangentPropagation" : true, "allowEdgeOverflow" : false});
        }
        {
            var Q0;
            {var subQ0=sQuery(id+"F0.wireOp",EDGE,"E10.0");Q0=makeQuery(id+"F1.opExtrude","CAP_EDGE",EDGE,{"disambiguationData":[OSD([subQ0]),TDD([makeQuery(id+"F0.imprint","IMPRINT",EDGE,{"disambiguationData":[TD([[makeQuery(id+"F0.imprint","INTERSECT",VERTEX,{"derivedFrom":[sQuery(id+"F0.wireOp",EDGE,"E5"),subQ0]}),1.0]])],"derivedFrom":subQ0})])],"isStart":false});}
            var Q1;
            {var subQ0=sQuery(id+"F0.wireOp",EDGE,"E9.0");Q1=makeQuery(id+"F1.opExtrude","CAP_EDGE",EDGE,{"disambiguationData":[OSD([subQ0]),TDD([makeQuery(id+"F0.imprint","IMPRINT",EDGE,{"disambiguationData":[TD([[makeQuery(id+"F0.imprint","INTERSECT",VERTEX,{"derivedFrom":[sQuery(id+"F0.wireOp",EDGE,"E5"),subQ0]}),1.0]])],"derivedFrom":subQ0})])],"isStart":false});}
            var Q2;
            {var subQ0=sQuery(id+"F0.wireOp",EDGE,"E8");Q2=makeQuery(id+"F1.opExtrude","CAP_EDGE",EDGE,{"disambiguationData":[OSD([subQ0]),TDD([makeQuery(id+"F0.imprint","IMPRINT",EDGE,{"disambiguationData":[TD([[makeQuery(id+"F0.imprint","INTERSECT",VERTEX,{"derivedFrom":[sQuery(id+"F0.wireOp",EDGE,"E5"),subQ0]}),1.0]])],"derivedFrom":subQ0})])],"isStart":false});}
            var Q3;
            {var subQ0=sQuery(id+"F0.wireOp",EDGE,"E7");Q3=makeQuery(id+"F1.opExtrude","CAP_EDGE",EDGE,{"disambiguationData":[OSD([subQ0]),TDD([makeQuery(id+"F0.imprint","IMPRINT",EDGE,{"disambiguationData":[TD([[makeQuery(id+"F0.imprint","INTERSECT",VERTEX,{"derivedFrom":[sQuery(id+"F0.wireOp",EDGE,"E5"),subQ0]}),1.0]])],"derivedFrom":subQ0})])],"isStart":false});}
            fillet(context, id + "F10", {"entities" : qUnion([Q0, Q1, Q2, Q3]), "radius" : 1 * mm, "tangentPropagation" : true, "allowEdgeOverflow" : false});
        }
        {
            var Q0;
            Q0=makeQuery(id+"F7.opLoft","SWEPT_FACE",FACE,{"disambiguationData":[OSD([sQuery(id+"F5.wireOp",EDGE,"E12.0"),sQuery(id+"F5.wireOp",EDGE,"E12.1"),sQuery(id+"F5.wireOp",EDGE,"E13"),sQuery(id+"F6.wireOp",EDGE,"E19.1"),sQuery(id+"F6.wireOp",EDGE,"E19.2"),sQuery(id+"F6.wireOp",EDGE,"E19.3")])]});
            var sketch = newSketch(context, id + "F11", { "sketchPlane" : qUnion([Q0])});
            skLineSegment(sketch, "E22.0.0", {"start": v(25.52, -12.58) * mm, "end": v(25.52, 33.97) * mm});
            skLineSegment(sketch, "E22.0.1", {"start": v(25.52, 33.97) * mm, "end": v(-22.48, 33.97) * mm});
            skLineSegment(sketch, "E22.0.2", {"start": v(-22.48, 33.97) * mm, "end": v(-22.48, -12.58) * mm});
            skLineSegment(sketch, "E22.0.3", {"start": v(-22.48, -12.58) * mm, "end": v(25.52, -12.58) * mm});
            skLineSegment(sketch, "E23.0", {"start": v(21.52, 29.97) * mm, "end": v(-18.48, 29.97) * mm});
            skLineSegment(sketch, "E23.1", {"start": v(21.52, -8.58) * mm, "end": v(21.52, 29.97) * mm});
            skLineSegment(sketch, "E23.2", {"start": v(-18.48, -8.58) * mm, "end": v(21.52, -8.58) * mm});
            skLineSegment(sketch, "E23.3", {"start": v(-18.48, 29.97) * mm, "end": v(-18.48, -8.58) * mm});
            skLineSegment(sketch, "E24.0", {"start": v(-0.48, 29.97) * mm, "end": v(-0.48, -8.58) * mm});
            skLineSegment(sketch, "E25.MirrorCS", {"start": v(3.52, 29.97) * mm, "end": v(3.52, -8.58) * mm});
            skLineSegment(sketch, "E26.0", {"start": v(-18.48, 8.7) * mm, "end": v(21.52, 8.7) * mm});
            skLineSegment(sketch, "E27.MirrorCS", {"start": v(-18.48, 12.7) * mm, "end": v(21.52, 12.7) * mm});
            skSolve(sketch);
        }
        {
            var Q0;
            {var subQ0=sQuery(id+"F11.wireOp",EDGE,"E23.3");var subQ1=sQuery(id+"F11.wireOp",EDGE,"E23.0");var subQ2=makeQuery(id+"F11.imprint","INTERSECT",VERTEX,{"derivedFrom":[subQ1,subQ0]});Q0=makeQuery(id+"F11.imprint","IMPRINT",FACE,{"disambiguationData":[TD([[makeQuery(id+"F11.imprint","IMPRINT",EDGE,{"disambiguationData":[TD([[subQ2,1.0]])],"derivedFrom":subQ1}),1.0]])]});}
            var Q1;
            {var subQ0=sQuery(id+"F11.wireOp",EDGE,"E23.1");var subQ1=sQuery(id+"F11.wireOp",EDGE,"E23.0");var subQ2=makeQuery(id+"F11.imprint","INTERSECT",VERTEX,{"derivedFrom":[subQ1,subQ0]});Q1=makeQuery(id+"F11.imprint","IMPRINT",FACE,{"disambiguationData":[TD([[makeQuery(id+"F11.imprint","IMPRINT",EDGE,{"disambiguationData":[TD([[subQ2,-1.0]])],"derivedFrom":subQ1}),1.0]])]});}
            var Q2;
            {var subQ0=sQuery(id+"F11.wireOp",EDGE,"E23.2");var subQ1=sQuery(id+"F11.wireOp",EDGE,"E23.1");var subQ2=makeQuery(id+"F11.imprint","INTERSECT",VERTEX,{"derivedFrom":[subQ1,subQ0]});Q2=makeQuery(id+"F11.imprint","IMPRINT",FACE,{"disambiguationData":[TD([[makeQuery(id+"F11.imprint","IMPRINT",EDGE,{"disambiguationData":[TD([[subQ2,-1.0]])],"derivedFrom":subQ1}),1.0]])]});}
            var Q3;
            {var subQ0=sQuery(id+"F11.wireOp",EDGE,"E23.3");var subQ1=sQuery(id+"F11.wireOp",EDGE,"E23.2");var subQ2=makeQuery(id+"F11.imprint","INTERSECT",VERTEX,{"derivedFrom":[subQ1,subQ0]});Q3=makeQuery(id+"F11.imprint","IMPRINT",FACE,{"disambiguationData":[TD([[makeQuery(id+"F11.imprint","IMPRINT",EDGE,{"disambiguationData":[TD([[subQ2,-1.0]])],"derivedFrom":subQ1}),1.0]])]});}
            extrude(context, id + "F12", {"entities" : qUnion([Q0, Q1, Q2, Q3]), "operationType" : NewBodyOperationType.REMOVE, "oppositeDirection" : true, "depth" : 4.4 * mm});
        }
        {
            var Q0;
            {var subQ0=sQuery(id+"F11.wireOp",EDGE,"E23.2");Q0=makeQuery(id+"F12.boolean.opBoolean","COPY",FACE,{"derivedFrom":makeQuery(id+"F12.opExtrude","SWEPT_FACE",FACE,{"disambiguationData":[OSD([subQ0]),TDD([makeQuery(id+"F11.imprint","IMPRINT",EDGE,{"disambiguationData":[TD([[makeQuery(id+"F11.imprint","INTERSECT",VERTEX,{"derivedFrom":[subQ0,sQuery(id+"F11.wireOp",EDGE,"E23.3")]}),-1.0]])],"derivedFrom":subQ0})])]})});}
            var Q1;
            {var subQ0=sQuery(id+"F11.wireOp",EDGE,"E23.2");Q1=makeQuery(id+"F12.boolean.opBoolean","COPY",FACE,{"derivedFrom":makeQuery(id+"F12.opExtrude","SWEPT_FACE",FACE,{"disambiguationData":[OSD([subQ0]),TDD([makeQuery(id+"F11.imprint","IMPRINT",EDGE,{"disambiguationData":[TD([[makeQuery(id+"F11.imprint","INTERSECT",VERTEX,{"derivedFrom":[sQuery(id+"F11.wireOp",EDGE,"E23.1"),subQ0]}),1.0]])],"derivedFrom":subQ0})])]})});}
            var Q2;
            Q2=makeQuery(id+"F12.boolean.opBoolean","COPY",FACE,{"derivedFrom":makeQuery(id+"F12.opExtrude","SWEPT_FACE",FACE,{"disambiguationData":[OSD([sQuery(id+"F11.wireOp",EDGE,"E27.MirrorCS")])]})});
            var Q3;
            Q3=makeQuery(id+"F1.opExtrude","SWEPT_FACE",FACE,{"disambiguationData":[OSD([sQuery(id+"F0.wireOp",EDGE,"E0.top")])]});
            var Q4;
            {var subQ0=sQuery(id+"F0.wireOp",EDGE,"E6");var subQ1=sQuery(id+"F0.wireOp",EDGE,"E4");var subQ2=sQuery(id+"F0.wireOp",EDGE,"E0.right");var subQ3=sQuery(id+"F0.wireOp",EDGE,"E0.left");var subQ4=sQuery(id+"F0.wireOp",EDGE,"E3");var subQ5=sQuery(id+"F0.wireOp",EDGE,"E2");Q4=makeQuery(id+"F8.opBoolean","MERGE",FACE,{"derivedFrom":[makeQuery(id+"F1.opExtrude","CAP_FACE",FACE,{"disambiguationData":[OSD([sQuery(id+"F0.wireOp",EDGE,"E0.bottom"),sQuery(id+"F0.wireOp",EDGE,"E0.top"),subQ3,subQ2,sQuery(id+"F0.wireOp",EDGE,"E1"),subQ5,subQ4,subQ1,sQuery(id+"F0.wireOp",EDGE,"E5"),subQ0,sQuery(id+"F0.wireOp",EDGE,"E7"),sQuery(id+"F0.wireOp",EDGE,"E8"),sQuery(id+"F0.wireOp",EDGE,"E9.0"),sQuery(id+"F0.wireOp",EDGE,"E10.0")])],"isStart":true}),makeQuery(id+"F2.opExtrude","CAP_FACE",FACE,{"disambiguationData":[OSD([subQ3,subQ2,subQ5,subQ4])],"isStart":true}),makeQuery(id+"F2.opExtrude","CAP_FACE",FACE,{"disambiguationData":[OSD([subQ3,subQ2,subQ1,subQ0])],"isStart":true})]});}
            var Q5;
            Q5=makeQuery(id+"F12.boolean.opBoolean","INTERSECT",EDGE,{"derivedFrom":[makeQuery(id+"F7.opLoft","SWEPT_FACE",FACE,{"disambiguationData":[OSD([sQuery(id+"F0.wireOp",EDGE,"E0.left"),sQuery(id+"F0.wireOp",EDGE,"E8"),sQuery(id+"F5.wireOp",EDGE,"E12.0"),sQuery(id+"F5.wireOp",EDGE,"E14"),sQuery(id+"F6.wireOp",EDGE,"E19.0"),sQuery(id+"F6.wireOp",EDGE,"E19.2")])]}),makeQuery(id+"F12.opExtrude","SWEPT_FACE",FACE,{"disambiguationData":[OSD([sQuery(id+"F11.wireOp",EDGE,"E23.0")])]})]});
            var Q6;
            {var subQ0=sQuery(id+"F11.wireOp",EDGE,"E23.0");Q6=makeQuery(id+"F12.boolean.opBoolean","COPY",EDGE,{"derivedFrom":makeQuery(id+"F12.opExtrude","CAP_EDGE",EDGE,{"disambiguationData":[OSD([subQ0]),TDD([makeQuery(id+"F11.imprint","IMPRINT",EDGE,{"disambiguationData":[TD([[makeQuery(id+"F11.imprint","INTERSECT",VERTEX,{"derivedFrom":[subQ0,sQuery(id+"F11.wireOp",EDGE,"E23.3")]}),1.0]])],"derivedFrom":subQ0})])],"isStart":true})});}
            var Q7;
            {var subQ0=sQuery(id+"F11.wireOp",EDGE,"E23.0");Q7=makeQuery(id+"F12.boolean.opBoolean","COPY",EDGE,{"derivedFrom":makeQuery(id+"F12.opExtrude","CAP_EDGE",EDGE,{"disambiguationData":[OSD([subQ0]),TDD([makeQuery(id+"F11.imprint","IMPRINT",EDGE,{"disambiguationData":[TD([[makeQuery(id+"F11.imprint","INTERSECT",VERTEX,{"derivedFrom":[subQ0,sQuery(id+"F11.wireOp",EDGE,"E23.1")]}),-1.0]])],"derivedFrom":subQ0})])],"isStart":true})});}
            fillet(context, id + "F13", {"entities" : qUnion([Q0, Q1, Q2, Q3, Q4, Q5, Q6, Q7]), "radius" : 1 * mm, "tangentPropagation" : true, "allowEdgeOverflow" : false});
        }
    });
